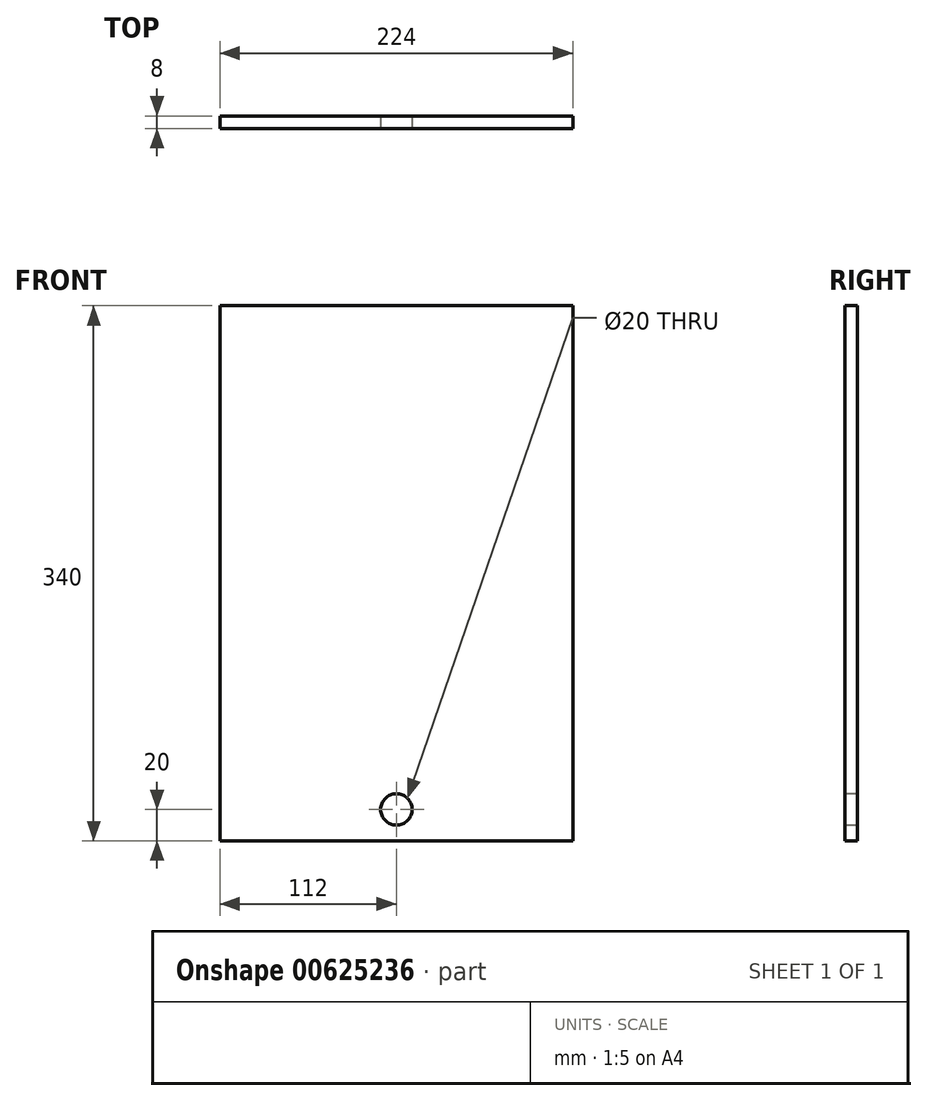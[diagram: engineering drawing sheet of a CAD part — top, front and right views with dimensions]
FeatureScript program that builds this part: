
annotation { "Feature Type Name" : "Feature", "Feature Type Description" : "" }
export const myFeature = defineFeature(function(context is Context, id is Id, definition is map)
    precondition{}
    {
        {
            var Q0;
            Q0=qCreatedBy(makeId("Front.planeOp"),FACE);
            var sketch = newSketch(context, id + "F0", { "sketchPlane" : qUnion([Q0])});
            skLineSegment(sketch, "E0.bottom", {"start": v(-112, 170) * mm, "end": v(112, 170) * mm});
            skLineSegment(sketch, "E0.top", {"start": v(-112, -170) * mm, "end": v(112, -170) * mm});
            skLineSegment(sketch, "E0.left", {"start": v(-112, 170) * mm, "end": v(-112, -170) * mm});
            skLineSegment(sketch, "E0.right", {"start": v(112, 170) * mm, "end": v(112, -170) * mm});
            skPoint(sketch, "E0.middle", {"position": v(0, 0) * mm});
            skSolve(sketch);
        }
        {
            var Q0;
            Q0=makeQuery(id+"F0.imprint","IMPRINT",FACE,{"disambiguationData":[TD([[makeQuery(id+"F0.imprint","IMPRINT",EDGE,{"derivedFrom":sQuery(id+"F0.wireOp",EDGE,"E0.bottom")}),-1.0]])]});
            var Q1;
            Q1=qSketchRegion(id+"F2",true);
            extrude(context, id + "F1", {"entities" : qUnion([Q0, Q1]), "depth" : 8 * mm, "offsetDistance" : 25 * mm});
        }
        {
            var Q0;
            Q0=makeQuery(id+"F1.opExtrude","CAP_FACE",FACE,{"disambiguationData":[OSD([sQuery(id+"F0.wireOp",EDGE,"E0.bottom"),sQuery(id+"F0.wireOp",EDGE,"E0.top"),sQuery(id+"F0.wireOp",EDGE,"E0.left"),sQuery(id+"F0.wireOp",EDGE,"E0.right")])],"isStart":false});
            var sketch = newSketch(context, id + "F2", { "sketchPlane" : qUnion([Q0])});
            skCircle(sketch, "E1", {"center": v(0, -150) * mm, "radius": 10 * mm});
            skSolve(sketch);
        }
        {
            var Q0;
            Q0=makeQuery(id+"F2.imprint","IMPRINT",FACE,{"disambiguationData":[TD([[makeQuery(id+"F2.imprint","IMPRINT",EDGE,{"derivedFrom":sQuery(id+"F2.wireOp",EDGE,"E1")}),1.0]])]});
            extrude(context, id + "F3", {"entities" : qUnion([Q0]), "operationType" : NewBodyOperationType.REMOVE, "endBound" : BoundingType.UP_TO_NEXT, "oppositeDirection" : true, "depth" : 25 * mm});
        }
    });
